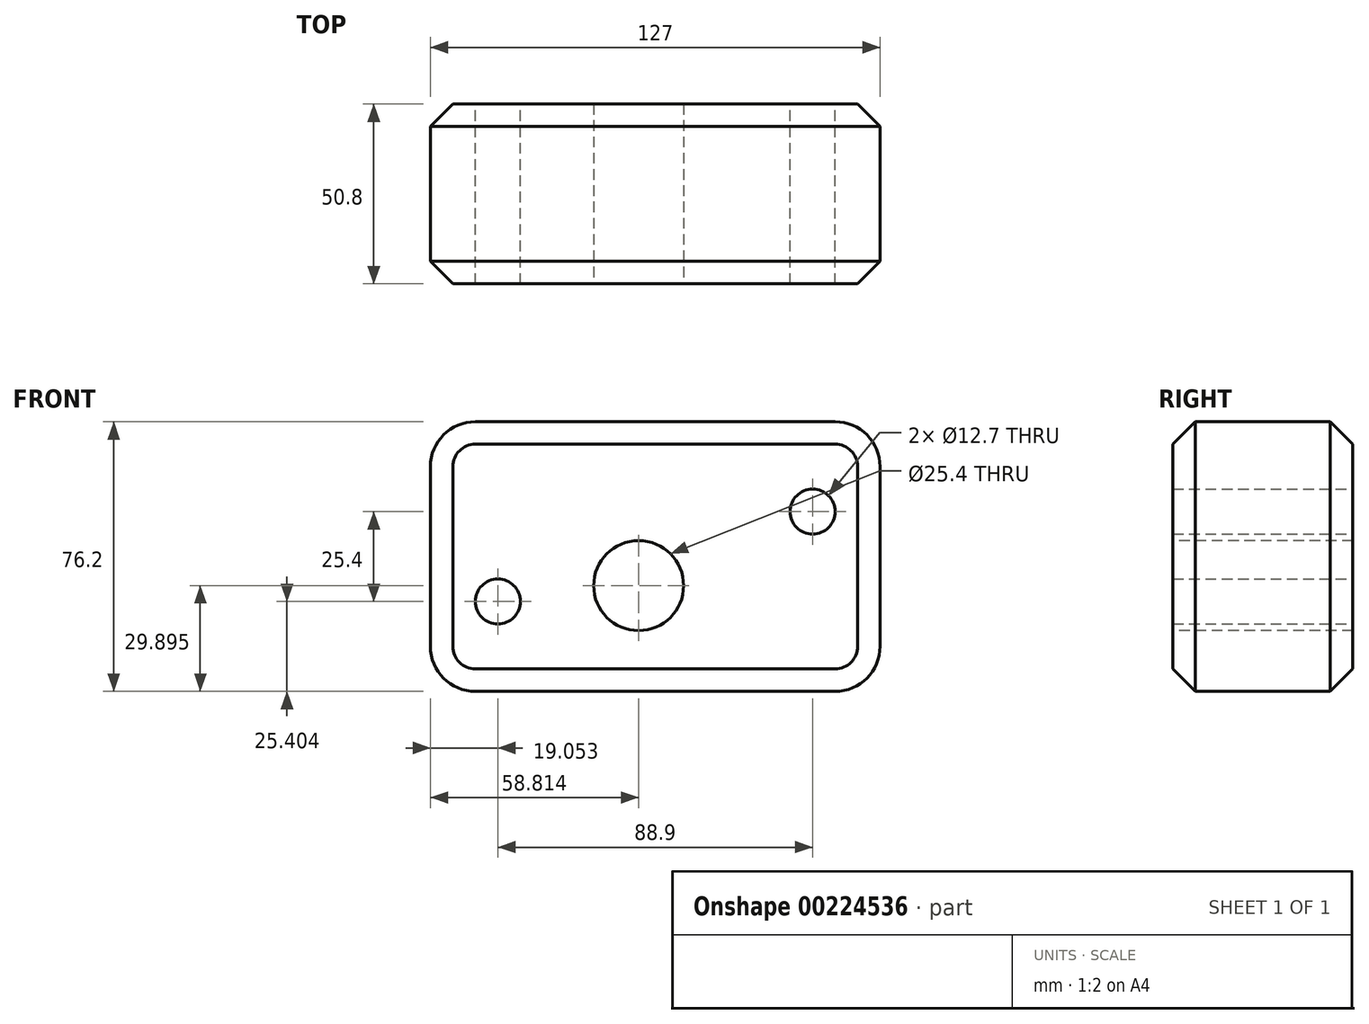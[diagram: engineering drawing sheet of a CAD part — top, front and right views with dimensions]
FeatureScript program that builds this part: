
annotation { "Feature Type Name" : "Feature", "Feature Type Description" : "" }
export const myFeature = defineFeature(function(context is Context, id is Id, definition is map)
    precondition{}
    {
        {
            var Q0;
            Q0=qCreatedBy(makeId("Front.planeOp"),FACE);
            var sketch = newSketch(context, id + "F0", { "sketchPlane" : qUnion([Q0])});
            skLineSegment(sketch, "E0.bottom", {"start": v(-64.75, 32.11) * mm, "end": v(62.25, 32.11) * mm});
            skLineSegment(sketch, "E0.top", {"start": v(-64.75, -44.09) * mm, "end": v(62.25, -44.09) * mm});
            skLineSegment(sketch, "E0.left", {"start": v(-64.75, 32.11) * mm, "end": v(-64.75, -44.09) * mm});
            skLineSegment(sketch, "E0.right", {"start": v(62.25, 32.11) * mm, "end": v(62.25, -44.09) * mm});
            skCircle(sketch, "E1", {"center": v(43.2, 6.71) * mm, "radius": 6.35 * mm});
            skCircle(sketch, "E2", {"center": v(-45.7, -18.69) * mm, "radius": 6.35 * mm});
            skSolve(sketch);
        }
        {
            var Q0;
            Q0=makeQuery(id+"F0.imprint","IMPRINT",FACE,{"disambiguationData":[TD([[makeQuery(id+"F0.imprint","IMPRINT",EDGE,{"derivedFrom":sQuery(id+"F0.wireOp",EDGE,"E0.bottom")}),-1.0]])]});
            extrude(context, id + "F1", {"entities" : qUnion([Q0]), "depth" : 50.8 * mm});
        }
        {
            var Q0;
            Q0=makeQuery(id+"F1.opExtrude","CAP_FACE",FACE,{"disambiguationData":[OSD([sQuery(id+"F0.wireOp",EDGE,"E0.bottom"),sQuery(id+"F0.wireOp",EDGE,"E0.top"),sQuery(id+"F0.wireOp",EDGE,"E0.left"),sQuery(id+"F0.wireOp",EDGE,"E0.right"),sQuery(id+"F0.wireOp",EDGE,"E1"),sQuery(id+"F0.wireOp",EDGE,"E2")])],"isStart":false});
            var sketch = newSketch(context, id + "F2", { "sketchPlane" : qUnion([Q0])});
            skCircle(sketch, "E3", {"center": v(-5.94, -14.2) * mm, "radius": 12.7 * mm});
            skSolve(sketch);
        }
        {
            var Q0;
            Q0 = qSketchRegion(id + "F2", true);
            extrude(context, id + "F3", {"entities" : qUnion([Q0]), "operationType" : NewBodyOperationType.REMOVE, "oppositeDirection" : true, "depth" : 60.45 * mm});
        }
        {
            var Q0;
            Q0=makeQuery(id+"F1.opExtrude","SWEPT_EDGE",EDGE,{"disambiguationData":[OSD([sQuery(id+"F0.wireOp",EDGE,"E0.bottom"),sQuery(id+"F0.wireOp",EDGE,"E0.left")])]});
            fillet(context, id + "F4", {"entities" : qUnion([Q0]), "radius" : 12.7 * mm, "tangentPropagation" : true, "allowEdgeOverflow" : false});
        }
        {
            var Q0;
            Q0=makeQuery(id+"F1.opExtrude","SWEPT_EDGE",EDGE,{"disambiguationData":[OSD([sQuery(id+"F0.wireOp",EDGE,"E0.bottom"),sQuery(id+"F0.wireOp",EDGE,"E0.right")])]});
            fillet(context, id + "F5", {"entities" : qUnion([Q0]), "radius" : 12.7 * mm, "tangentPropagation" : true, "allowEdgeOverflow" : false});
        }
        {
            var Q0;
            Q0=makeQuery(id+"F1.opExtrude","SWEPT_EDGE",EDGE,{"disambiguationData":[OSD([sQuery(id+"F0.wireOp",EDGE,"E0.top"),sQuery(id+"F0.wireOp",EDGE,"E0.right")])]});
            fillet(context, id + "F6", {"entities" : qUnion([Q0]), "radius" : 12.7 * mm, "tangentPropagation" : true, "allowEdgeOverflow" : false});
        }
        {
            var Q0;
            Q0=makeQuery(id+"F1.opExtrude","SWEPT_EDGE",EDGE,{"disambiguationData":[OSD([sQuery(id+"F0.wireOp",EDGE,"E0.top"),sQuery(id+"F0.wireOp",EDGE,"E0.left")])]});
            fillet(context, id + "F7", {"entities" : qUnion([Q0]), "radius" : 12.7 * mm, "tangentPropagation" : true, "allowEdgeOverflow" : false});
        }
        {
            var Q0;
            Q0=makeQuery(id+"F1.opExtrude","CAP_EDGE",EDGE,{"disambiguationData":[OSD([sQuery(id+"F0.wireOp",EDGE,"E0.bottom")])],"isStart":true});
            chamfer(context, id + "F8", {"entities" : qUnion([Q0]), "width" : 6.35 * mm, "tangentPropagation" : true});
        }
        {
            var Q0;
            Q0=makeQuery(id+"F1.opExtrude","CAP_EDGE",EDGE,{"disambiguationData":[OSD([sQuery(id+"F0.wireOp",EDGE,"E0.bottom")])],"isStart":false});
            chamfer(context, id + "F9", {"entities" : qUnion([Q0]), "width" : 6.35 * mm, "tangentPropagation" : true});
        }
    });
